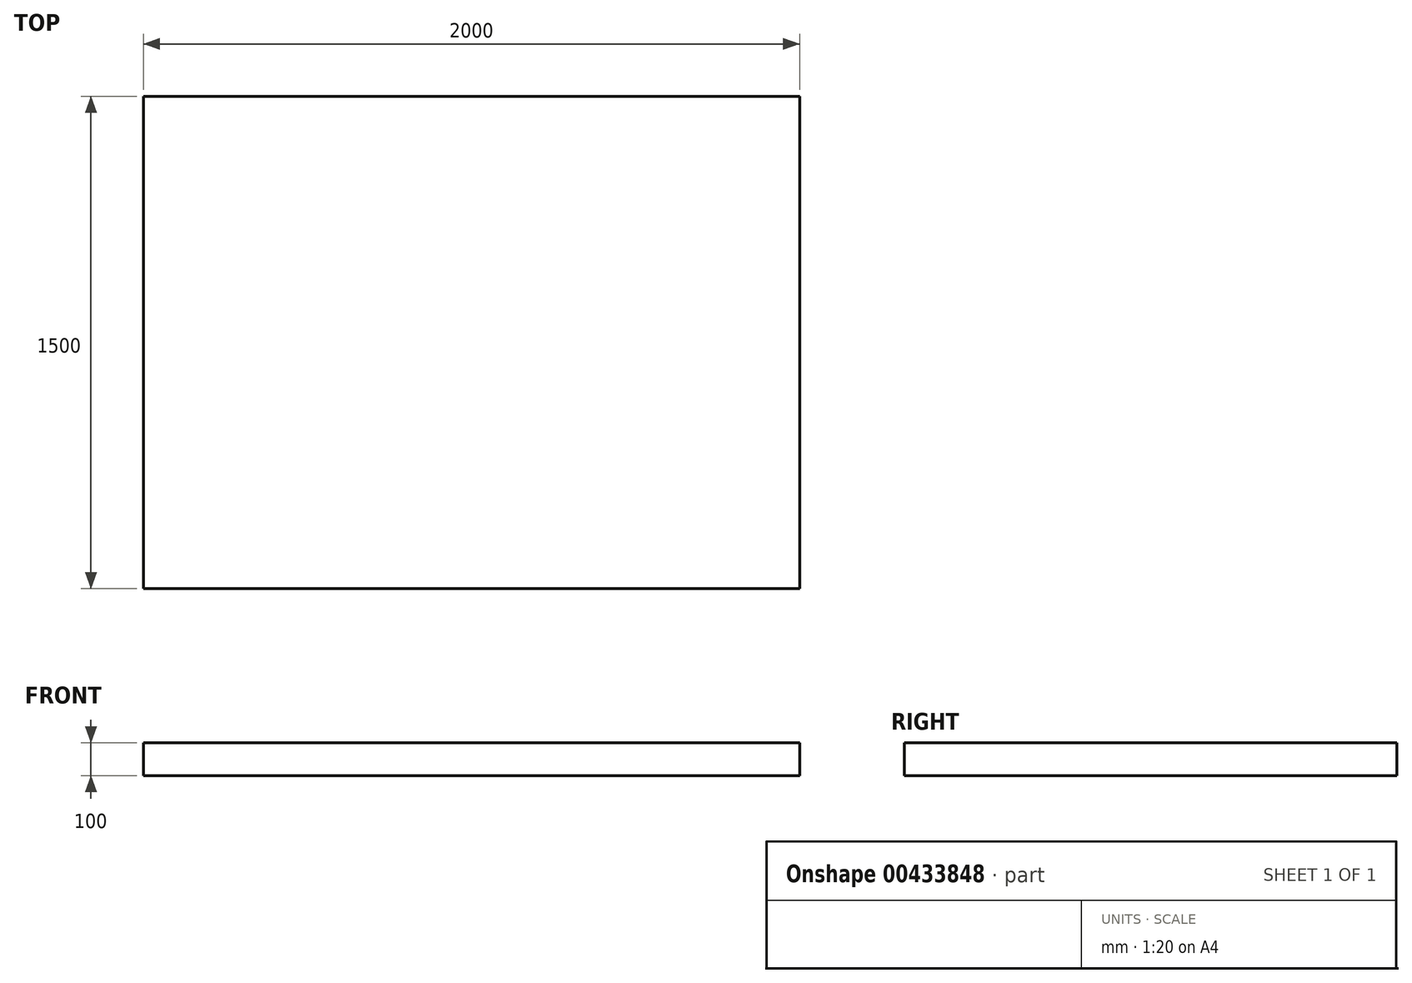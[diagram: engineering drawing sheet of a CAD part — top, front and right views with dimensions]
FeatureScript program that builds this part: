
annotation { "Feature Type Name" : "Feature", "Feature Type Description" : "" }
export const myFeature = defineFeature(function(context is Context, id is Id, definition is map)
    precondition{}
    {
        {
            var Q0;
            Q0=qCreatedBy(makeId("Top.planeOp"),FACE);
            var sketch = newSketch(context, id + "F0", { "sketchPlane" : qUnion([Q0])});
            skLineSegment(sketch, "E0.bottom", {"start": v(-1048.15, 791.84) * mm, "end": v(951.85, 791.84) * mm});
            skLineSegment(sketch, "E0.top", {"start": v(-1048.15, -708.16) * mm, "end": v(951.85, -708.16) * mm});
            skLineSegment(sketch, "E0.left", {"start": v(-1048.15, 791.84) * mm, "end": v(-1048.15, -708.16) * mm});
            skLineSegment(sketch, "E0.right", {"start": v(951.85, 791.84) * mm, "end": v(951.85, -708.16) * mm});
            skSolve(sketch);
        }
        {
            var Q0;
            Q0 = qSketchRegion(id + "F0", true);
            extrude(context, id + "F1", {"entities" : qUnion([Q0]), "oppositeDirection" : true, "depth" : 100 * mm});
        }
    });
